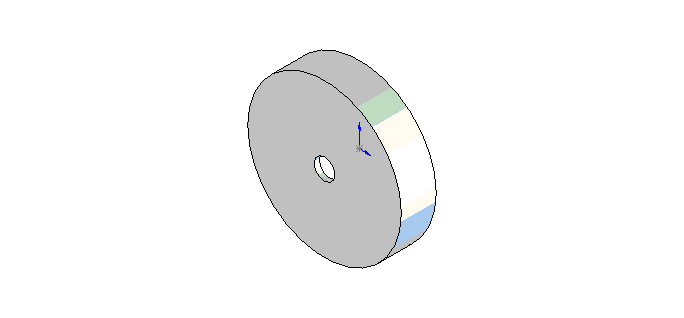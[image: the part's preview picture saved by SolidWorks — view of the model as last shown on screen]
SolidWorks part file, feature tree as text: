
SOLIDWORKS PART (.sldprt)
format: sldprt  version: not decoded by parser v0  size: 51,200 bytes
history: native  units: mm
features: plane x3, sketch x3, cut_extrude x2, extrude x1 + 1 further entry (+7 scaffold rows collapsed)
feature tree (17):
  scaffold x7  (default folders/planes/origin — collapsed)
  "Corps de surface"
  plane  "Face"
  plane  "Dessus"
  plane  "Droite"
  sketch  "Esquisse1"  dims[D1=~17.348914mm]
  extrude  "Extrusion1"  Depth=10mm
  sketch  "Esquisse2"  dims[D1=~20.059599mm]
  cut_extrude  "Enlèv. mat.-Extru.1"  Depth=8.5mm
  sketch  "Esquisse3"  dims[D1=~4.017758mm]
  cut_extrude  "Enlèv. mat.-Extru.3"  [1 undecoded]
decode coverage: 5 of 6 modeling features carry decoded parameters; 1 rows unclassified (native names shown)
note: ~ marks probable driven/reference dimensions
note: 1 parameter value undecoded
note: suppression state not decoded; provenance and decode notes live in map.json
